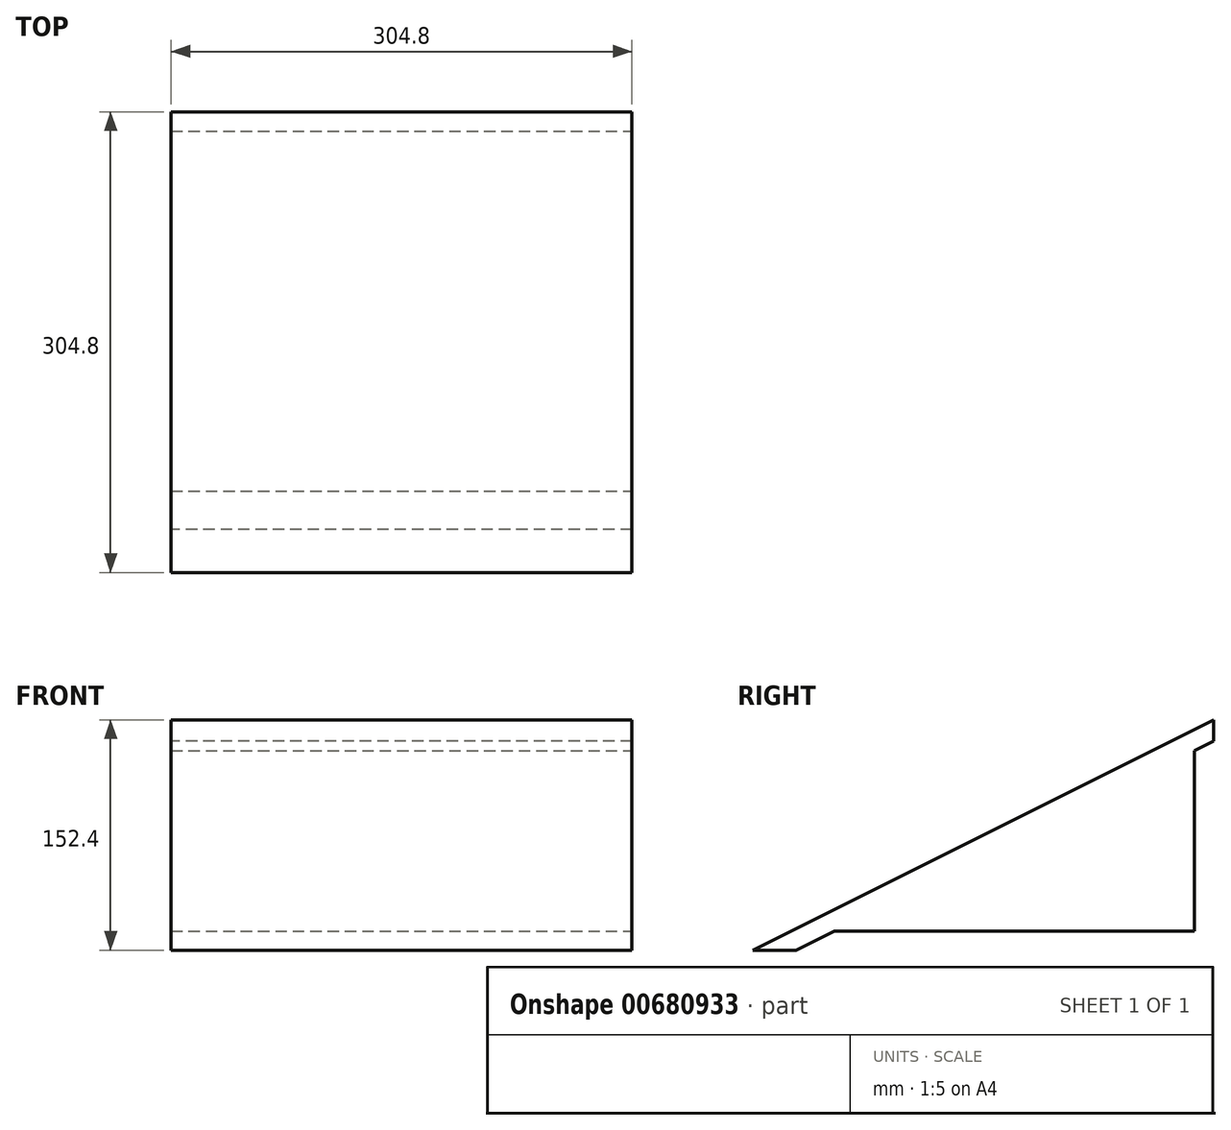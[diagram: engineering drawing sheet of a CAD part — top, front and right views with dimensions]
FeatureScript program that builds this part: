
annotation { "Feature Type Name" : "Feature", "Feature Type Description" : "" }
export const myFeature = defineFeature(function(context is Context, id is Id, definition is map)
    precondition{}
    {
        {
            var Q0;
            Q0=qCreatedBy(makeId("Right.planeOp"),FACE);
            var sketch = newSketch(context, id + "F0", { "sketchPlane" : qUnion([Q0])});
            skLineSegment(sketch, "E0.bottom", {"start": v(-152.4, 76.2) * mm, "end": v(152.4, 76.2) * mm});
            skLineSegment(sketch, "E0.top", {"start": v(-152.4, -76.2) * mm, "end": v(152.4, -76.2) * mm});
            skLineSegment(sketch, "E0.left", {"start": v(-152.4, 76.2) * mm, "end": v(-152.4, -76.2) * mm});
            skLineSegment(sketch, "E0.right", {"start": v(152.4, 76.2) * mm, "end": v(152.4, -76.2) * mm});
            skPoint(sketch, "E0.middle", {"position": v(0, 0) * mm});
            skLineSegment(sketch, "E1", {"start": v(-152.4, -76.2) * mm, "end": v(152.4, 76.2) * mm});
            skLineSegment(sketch, "E2", {"start": v(97.12, 34.36) * mm, "end": v(152.4, 62) * mm});
            skLineSegment(sketch, "E3", {"start": v(152.4, 62) * mm, "end": v(-124, -76.2) * mm});
            skLineSegment(sketch, "E4", {"start": v(-124, -76.2) * mm, "end": v(-129.68, -64.84) * mm});
            skLineSegment(sketch, "E5", {"start": v(152.4, 62) * mm, "end": v(146.72, 73.36) * mm});
            skLineSegment(sketch, "E6.bottom", {"start": v(152.4, 62) * mm, "end": v(139.7, 62) * mm});
            skLineSegment(sketch, "E6.top", {"start": v(152.4, -76.2) * mm, "end": v(139.7, -76.2) * mm});
            skLineSegment(sketch, "E6.left", {"start": v(152.4, 62) * mm, "end": v(152.4, -76.2) * mm});
            skLineSegment(sketch, "E6.right", {"start": v(139.7, 62) * mm, "end": v(139.7, -76.2) * mm});
            skLineSegment(sketch, "E7.bottom", {"start": v(-124, -76.2) * mm, "end": v(139.7, -76.2) * mm});
            skLineSegment(sketch, "E7.top", {"start": v(-124, -63.5) * mm, "end": v(139.7, -63.5) * mm});
            skLineSegment(sketch, "E7.left", {"start": v(-124, -76.2) * mm, "end": v(-124, -63.5) * mm});
            skLineSegment(sketch, "E7.right", {"start": v(139.7, -76.2) * mm, "end": v(139.7, -63.5) * mm});
            skSolve(sketch);
        }
        {
            var Q0;
            {var subQ0=sQuery(id+"F0.wireOp",EDGE,"E4");Q0=makeQuery(id+"F0.imprint","IMPRINT",FACE,{"disambiguationData":[TD([[makeQuery(id+"F0.imprint","IMPRINT",EDGE,{"derivedFrom":subQ0}),-1.0]])]});}
            var Q1;
            {var subQ0=sQuery(id+"F0.wireOp",EDGE,"E0.right");Q1=makeQuery(id+"F0.imprint","IMPRINT",FACE,{"disambiguationData":[TD([[makeQuery(id+"F0.imprint","IMPRINT",EDGE,{"derivedFrom":subQ0}),-1.0]])]});}
            var Q2;
            Q2=makeQuery(id+"F0.imprint","IMPRINT",FACE,{"disambiguationData":[TD([[makeQuery(id+"F0.imprint","IMPRINT",EDGE,{"derivedFrom":sQuery(id+"F0.wireOp",EDGE,"E6.top")}),-1.0]])]});
            var Q3;
            {var subQ0=sQuery(id+"F0.wireOp",EDGE,"E6.bottom");Q3=makeQuery(id+"F0.imprint","IMPRINT",FACE,{"disambiguationData":[TD([[makeQuery(id+"F0.imprint","IMPRINT",EDGE,{"derivedFrom":subQ0}),1.0]])]});}
            var Q4;
            {var subQ0=sQuery(id+"F0.wireOp",EDGE,"E0.top");Q4=makeQuery(id+"F0.imprint","IMPRINT",FACE,{"disambiguationData":[TD([[makeQuery(id+"F0.imprint","IMPRINT",EDGE,{"derivedFrom":subQ0}),1.0]])]});}
            var Q5;
            {var subQ0=sQuery(id+"F0.wireOp",EDGE,"E7.left");Q5=makeQuery(id+"F0.imprint","IMPRINT",FACE,{"disambiguationData":[TD([[makeQuery(id+"F0.imprint","IMPRINT",EDGE,{"derivedFrom":subQ0}),-1.0]])]});}
            var Q6;
            {var subQ0=sQuery(id+"F0.wireOp",EDGE,"E7.bottom");Q6=makeQuery(id+"F0.imprint","IMPRINT",FACE,{"disambiguationData":[TD([[makeQuery(id+"F0.imprint","IMPRINT",EDGE,{"derivedFrom":subQ0}),1.0]])]});}
            extrude(context, id + "F1", {"entities" : qUnion([Q0, Q1, Q2, Q3, Q4, Q5, Q6]), "depth" : 304.8 * mm, "offsetDistance" : 25.4 * mm});
        }
        {
            var Q0;
            Q0=makeQuery(id+"F1.opExtrude","CAP_FACE",FACE,{"disambiguationData":[OSD([sQuery(id+"F0.wireOp",EDGE,"E0.top"),sQuery(id+"F0.wireOp",EDGE,"E0.right"),sQuery(id+"F0.wireOp",EDGE,"E1"),sQuery(id+"F0.wireOp",EDGE,"E3"),sQuery(id+"F0.wireOp",EDGE,"E6.top"),sQuery(id+"F0.wireOp",EDGE,"E6.left"),sQuery(id+"F0.wireOp",EDGE,"E6.right"),sQuery(id+"F0.wireOp",EDGE,"E7.bottom"),sQuery(id+"F0.wireOp",EDGE,"E7.top")])],"isStart":false});
            var sketch = newSketch(context, id + "F2", { "sketchPlane" : qUnion([Q0])});
            skLineSegment(sketch, "E8", {"start": v(-98.6, -63.5) * mm, "end": v(139.7, 55.65) * mm});
            skLineSegment(sketch, "E9", {"start": v(139.7, 55.65) * mm, "end": v(139.7, -63.5) * mm});
            skLineSegment(sketch, "E10", {"start": v(139.7, -63.5) * mm, "end": v(-98.6, -63.5) * mm});
            skSolve(sketch);
        }
        {
            var Q0;
            Q0 = qSketchRegion(id + "F2", true);
            extrude(context, id + "F3", {"entities" : qUnion([Q0]), "operationType" : NewBodyOperationType.ADD, "oppositeDirection" : true, "depth" : 304.8 * mm, "offsetDistance" : 25.4 * mm});
        }
    });
